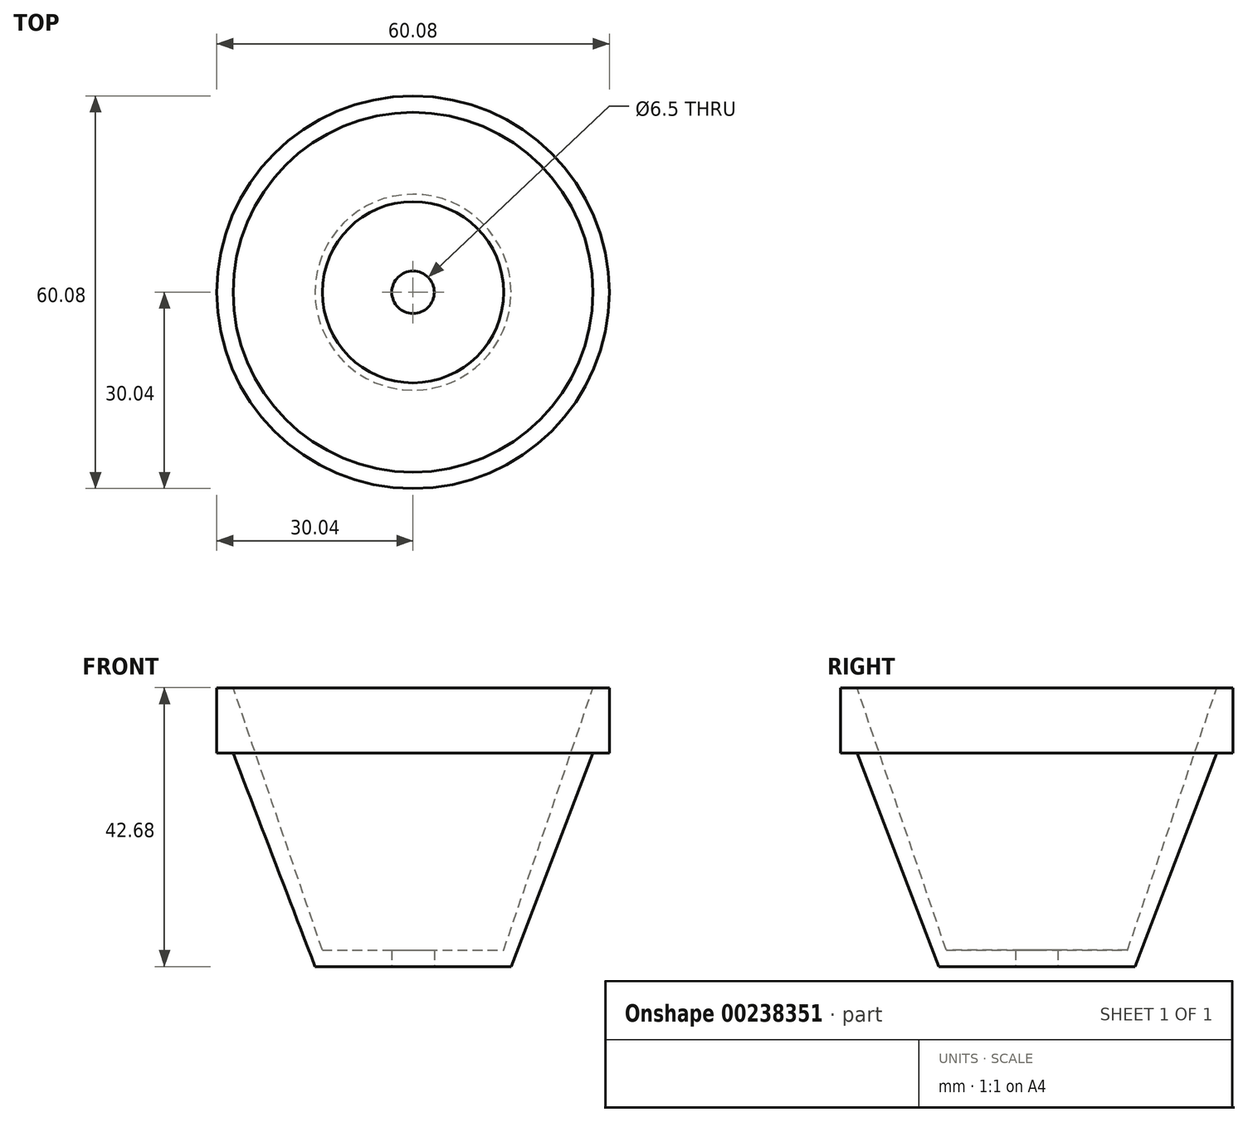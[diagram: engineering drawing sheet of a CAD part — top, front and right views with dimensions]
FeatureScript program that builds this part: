
annotation { "Feature Type Name" : "Feature", "Feature Type Description" : "" }
export const myFeature = defineFeature(function(context is Context, id is Id, definition is map)
    precondition{}
    {
        {
            var Q0;
            Q0=qCreatedBy(makeId("Front.planeOp"),FACE);
            var sketch = newSketch(context, id + "F0", { "sketchPlane" : qUnion([Q0])});
            skLineSegment(sketch, "E0", {"start": v(0, 0) * mm, "end": v(15, 0) * mm});
            skLineSegment(sketch, "E1", {"start": v(15, 0) * mm, "end": v(27.54, 32.68) * mm});
            skLineSegment(sketch, "E2", {"start": v(27.54, 32.68) * mm, "end": v(30.04, 32.68) * mm});
            skLineSegment(sketch, "E3", {"start": v(30.04, 32.68) * mm, "end": v(30.04, 42.68) * mm});
            skLineSegment(sketch, "E4", {"start": v(30.04, 42.68) * mm, "end": v(27.54, 42.68) * mm});
            skLineSegment(sketch, "E5", {"start": v(0, 2.5) * mm, "end": v(0, 0) * mm});
            skLineSegment(sketch, "E6", {"start": v(13.88, 2.5) * mm, "end": v(27.54, 42.68) * mm});
            skLineSegment(sketch, "E7", {"start": v(1.63, 2.5) * mm, "end": v(13.88, 2.5) * mm});
            skLineSegment(sketch, "E8", {"start": v(0, 0) * mm, "end": v(0, 42.68) * mm});
            skLineSegment(sketch, "E9", {"start": v(1.63, 0) * mm, "end": v(0, 0) * mm});
            skLineSegment(sketch, "E10", {"start": v(0, 2.5) * mm, "end": v(1.63, 2.5) * mm});
            skSolve(sketch);
        }
        {
            var Q0;
            Q0=makeQuery(id+"F0.imprint","IMPRINT",FACE,{"disambiguationData":[TD([[makeQuery(id+"F0.imprint","IMPRINT",EDGE,{"derivedFrom":sQuery(id+"F0.wireOp",EDGE,"E0")}),1.0]])]});
            var Q1;
            Q1=sQuery(id+"F0.wireOp",EDGE,"E8");
            revolve(context, id + "F1", {"entities" : qUnion([Q0]), "axis" : qUnion([Q1]), "revolveType" : RevolveType.FULL});
        }
        {
            var Q0;
            Q0=qCreatedBy(makeId("Top.planeOp"),FACE);
            var sketch = newSketch(context, id + "F2", { "sketchPlane" : qUnion([Q0])});
            skCircle(sketch, "E11", {"center": v(0, 0) * mm, "radius": 3.25 * mm});
            skSolve(sketch);
        }
        {
            var Q0;
            Q0 = qSketchRegion(id + "F2", true);
            extrude(context, id + "F3", {"entities" : qUnion([Q0]), "operationType" : NewBodyOperationType.REMOVE, "endBound" : BoundingType.THROUGH_ALL, "depth" : 25 * mm});
        }
    });
